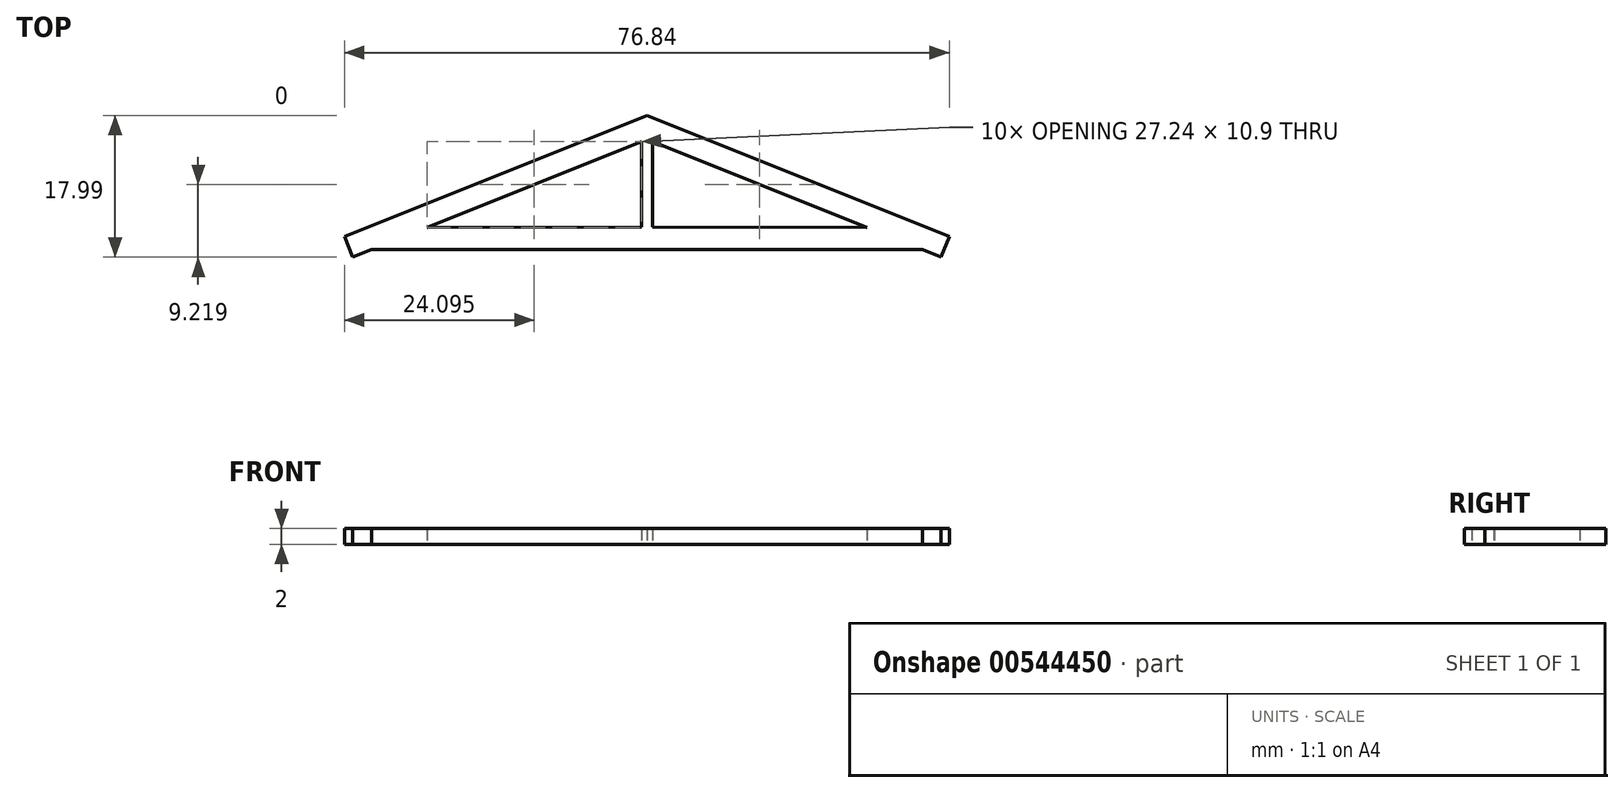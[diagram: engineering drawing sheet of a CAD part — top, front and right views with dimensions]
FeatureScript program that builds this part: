
annotation { "Feature Type Name" : "Feature", "Feature Type Description" : "" }
export const myFeature = defineFeature(function(context is Context, id is Id, definition is map)
    precondition{}
    {
        {
            var Q0;
            Q0=qCreatedBy(makeId("Top.planeOp"),FACE);
            var sketch = newSketch(context, id + "F0", { "sketchPlane" : qUnion([Q0])});
            skPoint(sketch, "E0", {"position": v(11.76, 0) * mm});
            skPoint(sketch, "E1", {"position": v(23.51, 0) * mm});
            skPoint(sketch, "E2.MirrorP", {"position": v(-11.76, 0) * mm});
            skPoint(sketch, "E3.MirrorP", {"position": v(-23.51, 0) * mm});
            skLineSegment(sketch, "E4.0", {"start": v(0, 15.63) * mm, "end": v(-35.8, 1.3) * mm});
            skLineSegment(sketch, "E5.0", {"start": v(0, 15.63) * mm, "end": v(35.8, 1.3) * mm});
            skLineSegment(sketch, "E6.MirrorCS", {"start": v(0.7, 12.3) * mm, "end": v(9.74, 8.7) * mm});
            skPoint(sketch, "E7.orphan", {"position": v(-1.05, 13) * mm});
            skPoint(sketch, "E8.orphan", {"position": v(1.05, 13) * mm});
            skLineSegment(sketch, "E9.0", {"start": v(-35.8, 1.3) * mm, "end": v(-38.42, 0.26) * mm});
            skLineSegment(sketch, "E10.0", {"start": v(35.8, 1.3) * mm, "end": v(38.42, 0.26) * mm});
            skLineSegment(sketch, "E11.MirrorCS", {"start": v(-35, -1.41) * mm, "end": v(-37.37, -2.36) * mm});
            skLineSegment(sketch, "E12.MirrorCS", {"start": v(35, -1.41) * mm, "end": v(37.37, -2.36) * mm});
            skLineSegment(sketch, "E13", {"start": v(-38.42, 0.26) * mm, "end": v(-37.37, -2.36) * mm});
            skLineSegment(sketch, "E14", {"start": v(37.37, -2.36) * mm, "end": v(38.42, 0.26) * mm});
            skPoint(sketch, "E15.orphan", {"position": v(-24.22, 3.47) * mm});
            skLineSegment(sketch, "E16", {"start": v(-11.05, 7.89) * mm, "end": v(-11.05, 7.94) * mm});
            skLineSegment(sketch, "E17.0", {"start": v(-0.7, 1.47) * mm, "end": v(-0.7, 12.3) * mm});
            skLineSegment(sketch, "E18", {"start": v(-10.93, 7.84) * mm, "end": v(-11.05, 7.94) * mm});
            skLineSegment(sketch, "E19.MirrorCS", {"start": v(0.7, 1.47) * mm, "end": v(0.7, 12.3) * mm});
            skLineSegment(sketch, "E20.MirrorCS", {"start": v(10.93, 7.84) * mm, "end": v(11.05, 7.94) * mm});
            skLineSegment(sketch, "E21.MirrorCS", {"start": v(11.05, 7.89) * mm, "end": v(11.05, 7.94) * mm});
            skPoint(sketch, "E22.orphan", {"position": v(0.7, 14.1) * mm});
            skPoint(sketch, "E23.orphan", {"position": v(-0.7, 14.1) * mm});
            skPoint(sketch, "E24.orphan", {"position": v(-35.27, 0) * mm});
            skLineSegment(sketch, "E25.0", {"start": v(-31.47, -1.41) * mm, "end": v(31.47, -1.41) * mm});
            skLineSegment(sketch, "E26", {"start": v(-31.47, -1.41) * mm, "end": v(-35, -1.41) * mm});
            skLineSegment(sketch, "E27", {"start": v(31.47, -1.41) * mm, "end": v(35, -1.41) * mm});
            skPoint(sketch, "E28.orphan", {"position": v(-22.8, 0) * mm});
            skPoint(sketch, "E29.orphan", {"position": v(-24.22, 0) * mm});
            skPoint(sketch, "E30.orphan", {"position": v(-13.66, 0) * mm});
            skPoint(sketch, "E31.orphan", {"position": v(-12.46, 1.04) * mm});
            skPoint(sketch, "E32.orphan", {"position": v(-11.05, 0) * mm});
            skPoint(sketch, "E33.orphan", {"position": v(-1.13, 0) * mm});
            skPoint(sketch, "E34.orphan", {"position": v(1.13, 0) * mm});
            skPoint(sketch, "E35.orphan", {"position": v(11.05, 0) * mm});
            skPoint(sketch, "E36.orphan", {"position": v(12.46, 1.04) * mm});
            skPoint(sketch, "E37.orphan", {"position": v(13.66, 0) * mm});
            skPoint(sketch, "E38.orphan", {"position": v(22.8, 0) * mm});
            skPoint(sketch, "E39.orphan", {"position": v(24.22, 0) * mm});
            skPoint(sketch, "E40.start.orphan", {"position": v(0, 0) * mm});
            skLineSegment(sketch, "E41.trimOffspring", {"start": v(-22.56, 3.56) * mm, "end": v(-22.8, 3.47) * mm});
            skLineSegment(sketch, "E42.trimOffspring", {"start": v(-24.22, 2.9) * mm, "end": v(-27.95, 1.41) * mm});
            skLineSegment(sketch, "E43", {"start": v(-27.95, 1.41) * mm, "end": v(-0.7, 1.47) * mm});
            skLineSegment(sketch, "E44", {"start": v(9.74, 8.7) * mm, "end": v(27.95, 1.41) * mm});
            skLineSegment(sketch, "E45", {"start": v(0.7, 1.47) * mm, "end": v(27.95, 1.41) * mm});
            skLineSegment(sketch, "E46", {"start": v(-0.7, 12.3) * mm, "end": v(-20.67, 4.32) * mm});
            skLineSegment(sketch, "E47.trimOffspring", {"start": v(-20.67, 4.32) * mm, "end": v(-24.22, 2.9) * mm});
            skSolve(sketch);
        }
        {
            var Q0;
            Q0=makeQuery(id+"F0.imprint","IMPRINT",FACE,{"disambiguationData":[TD([[makeQuery(id+"F0.imprint","IMPRINT",EDGE,{"derivedFrom":sQuery(id+"F0.wireOp",EDGE,"E4.0")}),1.0]])]});
            extrude(context, id + "F1", {"entities" : qUnion([Q0]), "depth" : 2 * mm, "offsetDistance" : 25 * mm});
        }
    });
